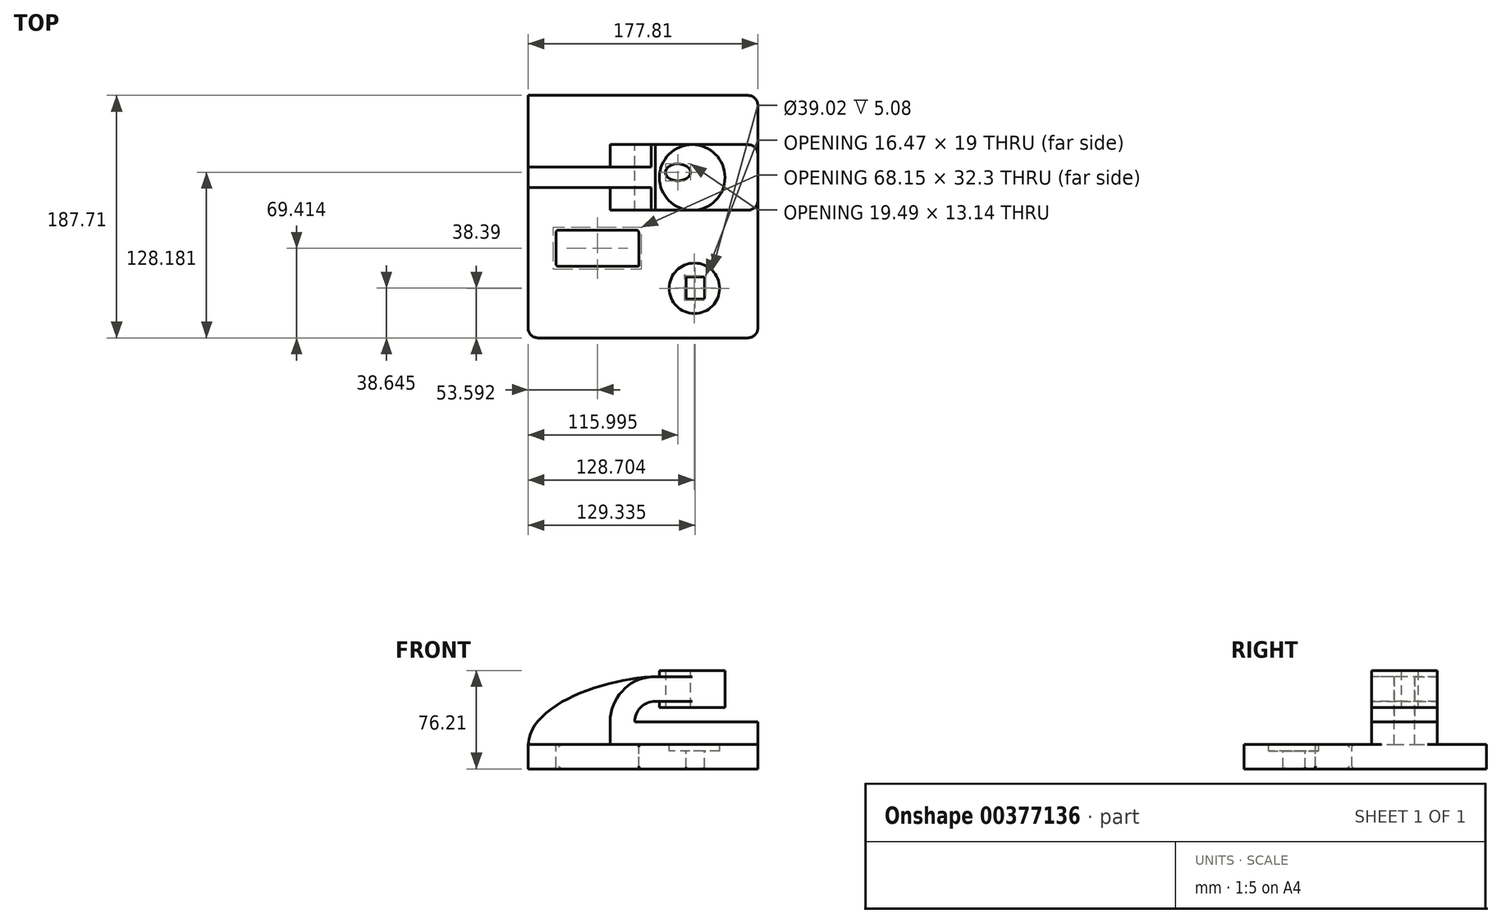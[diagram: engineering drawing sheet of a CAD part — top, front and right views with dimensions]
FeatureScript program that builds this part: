
annotation { "Feature Type Name" : "Feature", "Feature Type Description" : "" }
export const myFeature = defineFeature(function(context is Context, id is Id, definition is map)
    precondition{}
    {
        {
            var Q0;
            Q0=qCreatedBy(makeId("Front.planeOp"),FACE);
            var sketch = newSketch(context, id + "F0", { "sketchPlane" : qUnion([Q0])});
            skLineSegment(sketch, "E0.rect.bottom", {"start": v(-41.28, 9.52) * mm, "end": v(41.28, 9.52) * mm});
            skLineSegment(sketch, "E0.rect.top", {"start": v(-41.28, -9.52) * mm, "end": v(41.28, -9.52) * mm});
            skLineSegment(sketch, "E0.rect.left", {"start": v(-41.28, 9.52) * mm, "end": v(-41.28, -9.52) * mm});
            skLineSegment(sketch, "E0.rect.right", {"start": v(41.28, 9.52) * mm, "end": v(41.28, -9.52) * mm});
            skPoint(sketch, "E0.rect.middle", {"position": v(0, 0) * mm});
            skLineSegment(sketch, "E1", {"start": v(41.28, 9.52) * mm, "end": v(41.28, 27) * mm});
            skArc(sketch, "E2", {"start": v(41.28, 27) * mm, "mid": v(45.92, 38.23) * mm, "end": v(57.15, 42.88) * mm});
            skLineSegment(sketch, "E3", {"start": v(57.15, 42.88) * mm, "end": v(85.72, 42.88) * mm});
            skLineSegment(sketch, "E4.rect.bottom", {"start": v(60.32, 38.1) * mm, "end": v(111.12, 38.1) * mm});
            skLineSegment(sketch, "E4.rect.top", {"start": v(60.32, 66.68) * mm, "end": v(111.12, 66.68) * mm});
            skLineSegment(sketch, "E4.rect.left", {"start": v(60.32, 38.1) * mm, "end": v(60.32, 66.68) * mm});
            skLineSegment(sketch, "E4.rect.right", {"start": v(111.13, 38.1) * mm, "end": v(111.12, 66.68) * mm});
            skPoint(sketch, "E4.rect.middle", {"position": v(85.72, 52.39) * mm});
            skLineSegment(sketch, "E5.0", {"start": v(57.15, 61.93) * mm, "end": v(85.72, 61.93) * mm});
            skArc(sketch, "E5.1", {"start": v(22.23, 27) * mm, "mid": v(32.45, 51.7) * mm, "end": v(57.15, 61.93) * mm});
            skLineSegment(sketch, "E5.2", {"start": v(22.23, 9.52) * mm, "end": v(22.23, 27) * mm});
            skLineSegment(sketch, "E6", {"start": v(85.72, 38.1) * mm, "end": v(85.72, 66.68) * mm});
            skFitSpline(sketch, "E7", {"points": [v(-41.28, 9.53) * mm, v(57.15, 61.93) * mm], "startDerivative": vector(5.2, 92.34) * mm, "endDerivative": vector(120.92, 4.22) * mm});
            skSolve(sketch);
        }
        {
            var Q0;
            Q0=makeQuery(id+"F0.imprint","IMPRINT",FACE,{"disambiguationData":[TD([[makeQuery(id+"F0.imprint","IMPRINT",EDGE,{"derivedFrom":sQuery(id+"F0.wireOp",EDGE,"E0.rect.top")}),1.0]])]});
            extrude(context, id + "F1", {"entities" : qUnion([Q0]), "endBound" : BoundingType.SYMMETRIC, "depth" : 127 * mm});
        }
        {
            var Q0;
            {var subQ9=sQuery(id+"F0.wireOp",EDGE,"E1");Q0=makeQuery(id+"F0.imprint","IMPRINT",FACE,{"disambiguationData":[TD([[makeQuery(id+"F0.imprint","IMPRINT",EDGE,{"derivedFrom":subQ9}),1.0]])]});}
            var Q1;
            {var subQ0=sQuery(id+"F0.wireOp",EDGE,"E6");var subQ1=sQuery(id+"F0.wireOp",EDGE,"E3");var subQ2=makeQuery(id+"F0.imprint","INTERSECT",VERTEX,{"derivedFrom":[subQ1,subQ0]});Q1=makeQuery(id+"F0.imprint","IMPRINT",FACE,{"disambiguationData":[TD([[makeQuery(id+"F0.imprint","IMPRINT",EDGE,{"disambiguationData":[TD([[subQ2,1.0]])],"derivedFrom":subQ1}),1.0]])]});}
            extrude(context, id + "F2", {"entities" : qUnion([Q0, Q1]), "operationType" : NewBodyOperationType.ADD, "endBound" : BoundingType.SYMMETRIC, "depth" : 50.8 * mm});
        }
        {
            var Q0;
            {var subQ3=sQuery(id+"F0.wireOp",EDGE,"E5.2");Q0=makeQuery(id+"F0.imprint","IMPRINT",FACE,{"disambiguationData":[TD([[makeQuery(id+"F0.imprint","IMPRINT",EDGE,{"derivedFrom":subQ3}),1.0]])]});}
            extrude(context, id + "F3", {"entities" : qUnion([Q0]), "operationType" : NewBodyOperationType.ADD, "endBound" : BoundingType.SYMMETRIC, "depth" : 15.88 * mm});
        }
        {
            var Q0;
            {var subQ5=sQuery(id+"F0.wireOp",EDGE,"E4.rect.right");Q0=makeQuery(id+"F0.imprint","IMPRINT",FACE,{"disambiguationData":[TD([[makeQuery(id+"F0.imprint","IMPRINT",EDGE,{"derivedFrom":subQ5}),1.0]])]});}
            var Q1;
            Q1=sQuery(id+"F0.wireOp",EDGE,"E6");
            revolve(context, id + "F4", {"operationType" : NewBodyOperationType.ADD, "entities" : qUnion([Q0]), "axis" : qUnion([Q1]), "revolveType" : RevolveType.FULL});
        }
        {
            var Q0;
            Q0=makeQuery(id+"F2.boolean.opBoolean","MERGE",FACE,{"derivedFrom":[makeQuery(id+"F1.opExtrude","SWEPT_FACE",FACE,{"disambiguationData":[OSD([sQuery(id+"F0.wireOp",EDGE,"E0.rect.right")])]}),makeQuery(id+"F2.opExtrude","SWEPT_FACE",FACE,{"disambiguationData":[OSD([sQuery(id+"F0.wireOp",EDGE,"E1")])]})]});
            extrude(context, id + "F5", {"entities" : qUnion([Q0]), "operationType" : NewBodyOperationType.ADD, "depth" : 95.25 * mm});
        }
        {
            var Q0;
            {var subQ0=sQuery(id+"F0.wireOp",EDGE,"E0.rect.right");Q0=makeQuery(id+"F5.boolean.opBoolean","MERGE",FACE,{"derivedFrom":[makeQuery(id+"F1.opExtrude","CAP_FACE",FACE,{"disambiguationData":[OSD([sQuery(id+"F0.wireOp",EDGE,"E0.rect.bottom"),sQuery(id+"F0.wireOp",EDGE,"E0.rect.top"),sQuery(id+"F0.wireOp",EDGE,"E0.rect.left"),subQ0])],"isStart":false}),makeQuery(id+"F5.opExtrude","SWEPT_FACE",FACE,{"disambiguationData":[OSD([subQ0]),TDD([makeQuery(id+"F1.opExtrude","CAP_EDGE",EDGE,{"disambiguationData":[OSD([subQ0])],"isStart":false})])]})]});}
            extrude(context, id + "F6", {"entities" : qUnion([Q0]), "operationType" : NewBodyOperationType.ADD, "depth" : 60.7 * mm});
        }
        {
            var Q0;
            {var subQ0=sQuery(id+"F0.wireOp",EDGE,"E1");var subQ1=sQuery(id+"F0.wireOp",EDGE,"E0.rect.right");var subQ2=sQuery(id+"F0.wireOp",EDGE,"E0.rect.bottom");var subQ7=sQuery(id+"F0.wireOp",EDGE,"E0.rect.left");var subQ8=makeQuery(id+"F1.opExtrude","CAP_FACE",FACE,{"disambiguationData":[OSD([subQ2,sQuery(id+"F0.wireOp",EDGE,"E0.rect.top"),subQ7,subQ1])],"isStart":false});var subQ10=makeQuery(id+"F1.opExtrude","SWEPT_FACE",FACE,{"disambiguationData":[OSD([subQ2])]});Q0=makeQuery(id+"F6.boolean.opBoolean","MERGE",FACE,{"derivedFrom":[makeQuery(id+"F5.boolean.opBoolean","MERGE",FACE,{"derivedFrom":[makeQuery(id+"F3.boolean.opBoolean","SPLIT",FACE,{"disambiguationData":[TD([subQ8])],"derivedFrom":subQ10}),makeQuery(id+"F5.opExtrude","SWEPT_FACE",FACE,{"disambiguationData":[OSD([subQ2,subQ1,subQ0]),TDD([makeQuery(id+"F2.boolean.opBoolean","SPLIT",EDGE,{"disambiguationData":[TD([subQ8])],"derivedFrom":makeQuery(id+"F1.opExtrude","SWEPT_EDGE",EDGE,{"disambiguationData":[OSD([subQ2,subQ1,subQ0])]})})])]})]}),makeQuery(id+"F6.opExtrude","SWEPT_FACE",FACE,{"disambiguationData":[OSD([subQ2,subQ1,subQ0])]})]});}
            var sketch = newSketch(context, id + "F7", { "sketchPlane" : qUnion([Q0])});
            skLineSegment(sketch, "E8.bottom", {"start": v(44.37, -68.92) * mm, "end": v(-19.73, -68.92) * mm});
            skLineSegment(sketch, "E8.top", {"start": v(44.37, -40.68) * mm, "end": v(-19.73, -40.68) * mm});
            skLineSegment(sketch, "E8.left", {"start": v(44.37, -68.92) * mm, "end": v(44.37, -40.68) * mm});
            skLineSegment(sketch, "E8.right", {"start": v(-19.73, -68.92) * mm, "end": v(-19.73, -40.68) * mm});
            skPoint(sketch, "E8.middle", {"position": v(12.32, -54.8) * mm});
            skSolve(sketch);
        }
        {
            var Q0;
            Q0=makeQuery(id+"F7.imprint","IMPRINT",FACE,{"disambiguationData":[TD([[makeQuery(id+"F7.imprint","IMPRINT",EDGE,{"derivedFrom":sQuery(id+"F7.wireOp",EDGE,"E8.bottom")}),-1.0]])]});
            extrude(context, id + "F8", {"entities" : qUnion([Q0]), "operationType" : NewBodyOperationType.REMOVE, "oppositeDirection" : true, "depth" : 25.4 * mm});
        }
        {
            var Q0;
            {var subQ0=sQuery(id+"F0.wireOp",EDGE,"E1");var subQ1=sQuery(id+"F0.wireOp",EDGE,"E0.rect.right");var subQ2=sQuery(id+"F0.wireOp",EDGE,"E0.rect.bottom");var subQ7=sQuery(id+"F0.wireOp",EDGE,"E0.rect.left");var subQ8=makeQuery(id+"F1.opExtrude","CAP_FACE",FACE,{"disambiguationData":[OSD([subQ2,sQuery(id+"F0.wireOp",EDGE,"E0.rect.top"),subQ7,subQ1])],"isStart":false});var subQ10=makeQuery(id+"F1.opExtrude","SWEPT_FACE",FACE,{"disambiguationData":[OSD([subQ2])]});Q0=makeQuery(id+"F6.boolean.opBoolean","MERGE",FACE,{"derivedFrom":[makeQuery(id+"F5.boolean.opBoolean","MERGE",FACE,{"derivedFrom":[makeQuery(id+"F3.boolean.opBoolean","SPLIT",FACE,{"disambiguationData":[TD([subQ8])],"derivedFrom":subQ10}),makeQuery(id+"F5.opExtrude","SWEPT_FACE",FACE,{"disambiguationData":[OSD([subQ2,subQ1,subQ0]),TDD([makeQuery(id+"F2.boolean.opBoolean","SPLIT",EDGE,{"disambiguationData":[TD([subQ8])],"derivedFrom":makeQuery(id+"F1.opExtrude","SWEPT_EDGE",EDGE,{"disambiguationData":[OSD([subQ2,subQ1,subQ0])]})})])]})]}),makeQuery(id+"F6.opExtrude","SWEPT_FACE",FACE,{"disambiguationData":[OSD([subQ2,subQ1,subQ0])]})]});}
            var sketch = newSketch(context, id + "F9", { "sketchPlane" : qUnion([Q0])});
            skCircle(sketch, "E9", {"center": v(87.42, -85.82) * mm, "radius": 19.5 * mm});
            skPoint(sketch, "E9.first.point", {"position": v(99.6, -70.58) * mm});
            skPoint(sketch, "E9.second.point", {"position": v(68.56, -90.8) * mm});
            skPoint(sketch, "E9.third.point", {"position": v(68.2, -82.5) * mm});
            skSolve(sketch);
        }
        {
            var Q0;
            Q0=makeQuery(id+"F9.imprint","IMPRINT",FACE,{"disambiguationData":[TD([[makeQuery(id+"F9.imprint","IMPRINT",EDGE,{"derivedFrom":sQuery(id+"F9.wireOp",EDGE,"E9")}),1.0]])]});
            extrude(context, id + "F10", {"entities" : qUnion([Q0]), "operationType" : NewBodyOperationType.REMOVE, "oppositeDirection" : true, "depth" : 5.08 * mm});
        }
        {
            var Q0;
            {var subQ0=sQuery(id+"F0.wireOp",EDGE,"E1");var subQ1=sQuery(id+"F0.wireOp",EDGE,"E0.rect.right");var subQ2=sQuery(id+"F0.wireOp",EDGE,"E0.rect.bottom");var subQ7=sQuery(id+"F0.wireOp",EDGE,"E0.rect.left");var subQ8=makeQuery(id+"F1.opExtrude","CAP_FACE",FACE,{"disambiguationData":[OSD([subQ2,sQuery(id+"F0.wireOp",EDGE,"E0.rect.top"),subQ7,subQ1])],"isStart":false});var subQ10=makeQuery(id+"F1.opExtrude","SWEPT_FACE",FACE,{"disambiguationData":[OSD([subQ2])]});Q0=makeQuery(id+"F6.boolean.opBoolean","MERGE",FACE,{"derivedFrom":[makeQuery(id+"F5.boolean.opBoolean","MERGE",FACE,{"derivedFrom":[makeQuery(id+"F3.boolean.opBoolean","SPLIT",FACE,{"disambiguationData":[TD([subQ8])],"derivedFrom":subQ10}),makeQuery(id+"F5.opExtrude","SWEPT_FACE",FACE,{"disambiguationData":[OSD([subQ2,subQ1,subQ0]),TDD([makeQuery(id+"F2.boolean.opBoolean","SPLIT",EDGE,{"disambiguationData":[TD([subQ8])],"derivedFrom":makeQuery(id+"F1.opExtrude","SWEPT_EDGE",EDGE,{"disambiguationData":[OSD([subQ2,subQ1,subQ0])]})})])]})]}),makeQuery(id+"F6.opExtrude","SWEPT_FACE",FACE,{"disambiguationData":[OSD([subQ2,subQ1,subQ0])]})]});}
            var sketch = newSketch(context, id + "F11", { "sketchPlane" : qUnion([Q0])});
            skLineSegment(sketch, "E10.bottom", {"start": v(95.28, -77.08) * mm, "end": v(80.84, -77.08) * mm});
            skLineSegment(sketch, "E10.top", {"start": v(95.28, -94.05) * mm, "end": v(80.84, -94.05) * mm});
            skLineSegment(sketch, "E10.left", {"start": v(95.28, -77.08) * mm, "end": v(95.28, -94.05) * mm});
            skLineSegment(sketch, "E10.right", {"start": v(80.84, -77.08) * mm, "end": v(80.84, -94.05) * mm});
            skSolve(sketch);
        }
        {
            var Q0;
            Q0=makeQuery(id+"F11.imprint","IMPRINT",FACE,{"disambiguationData":[TD([[makeQuery(id+"F11.imprint","IMPRINT",EDGE,{"derivedFrom":sQuery(id+"F11.wireOp",EDGE,"E10.bottom")}),1.0]])]});
            extrude(context, id + "F12", {"entities" : qUnion([Q0]), "operationType" : NewBodyOperationType.REMOVE, "oppositeDirection" : true, "depth" : 25.4 * mm});
        }
        {
            var Q0;
            Q0=makeQuery(id+"F4.opRevolve","SWEPT_FACE",FACE,{"disambiguationData":[OSD([sQuery(id+"F0.wireOp",EDGE,"E4.rect.top")])]});
            var sketch = newSketch(context, id + "F13", { "sketchPlane" : qUnion([Q0])});
            skEllipse(sketch, "E11", {"center": v(74.71, 3.97) * mm, "majorRadius": 9.75 * mm, "minorRadius": 6.57 * mm, "majorAxis": v(1, 0)});
            skSolve(sketch);
        }
        {
            var Q0;
            Q0=makeQuery(id+"F13.imprint","IMPRINT",FACE,{"disambiguationData":[TD([[makeQuery(id+"F13.imprint","IMPRINT",EDGE,{"derivedFrom":sQuery(id+"F13.wireOp",EDGE,"E11")}),1.0]])]});
            var Q1;
            Q1=sQuery(id+"F13.wireOp",EDGE,"E11");
            extrude(context, id + "F14", {"entities" : qUnion([Q0]), "operationType" : NewBodyOperationType.REMOVE, "surfaceEntities" : qUnion([Q1]), "endBound" : BoundingType.UP_TO_NEXT, "oppositeDirection" : true, "depth" : 25.4 * mm});
        }
        {
            var Q0;
            Q0=makeQuery(id+"F6.opExtrude","CAP_EDGE",EDGE,{"disambiguationData":[OSD([sQuery(id+"F0.wireOp",EDGE,"E0.rect.left")])],"isStart":false});
            var Q1;
            Q1=makeQuery(id+"F6.opExtrude","CAP_EDGE",EDGE,{"disambiguationData":[OSD([sQuery(id+"F0.wireOp",EDGE,"E0.rect.right")])],"isStart":false});
            var Q2;
            {var subQ0=sQuery(id+"F0.wireOp",EDGE,"E1");Q2=makeQuery(id+"F5.opExtrude","CAP_EDGE",EDGE,{"disambiguationData":[OSD([subQ0]),TDD([makeQuery(id+"F2.opExtrude","CAP_EDGE",EDGE,{"disambiguationData":[OSD([subQ0])],"isStart":false})])],"isStart":false});}
            var Q3;
            {var subQ0=sQuery(id+"F0.wireOp",EDGE,"E1");Q3=makeQuery(id+"F5.opExtrude","CAP_EDGE",EDGE,{"disambiguationData":[OSD([subQ0]),TDD([makeQuery(id+"F2.opExtrude","CAP_EDGE",EDGE,{"disambiguationData":[OSD([subQ0])],"isStart":true})])],"isStart":false});}
            var Q4;
            {var subQ0=sQuery(id+"F0.wireOp",EDGE,"E0.rect.right");Q4=makeQuery(id+"F5.opExtrude","CAP_EDGE",EDGE,{"disambiguationData":[OSD([subQ0]),TDD([makeQuery(id+"F1.opExtrude","CAP_EDGE",EDGE,{"disambiguationData":[OSD([subQ0])],"isStart":true})])],"isStart":false});}
            fillet(context, id + "F15", {"entities" : qUnion([Q0, Q1, Q2, Q3, Q4]), "radius" : 7.62 * mm, "tangentPropagation" : true, "allowEdgeOverflow" : false});
        }
        {
            var Q0;
            Q0=makeQuery(id+"F8.boolean.opBoolean","COPY",FACE,{"derivedFrom":makeQuery(id+"F8.opExtrude","SWEPT_FACE",FACE,{"disambiguationData":[OSD([sQuery(id+"F7.wireOp",EDGE,"E8.right")])]})});
            var Q1;
            Q1=makeQuery(id+"F8.boolean.opBoolean","COPY",FACE,{"derivedFrom":makeQuery(id+"F8.opExtrude","SWEPT_FACE",FACE,{"disambiguationData":[OSD([sQuery(id+"F7.wireOp",EDGE,"E8.top")])]})});
            fillet(context, id + "F16", {"entities" : qUnion([Q0, Q1]), "radius" : 2.03 * mm, "tangentPropagation" : true, "allowEdgeOverflow" : false});
        }
        {
            var Q0;
            Q0=makeQuery(id+"F12.boolean.opBoolean","INTERSECT",EDGE,{"derivedFrom":[makeQuery(id+"F10.boolean.opBoolean","COPY",FACE,{"derivedFrom":makeQuery(id+"F10.opExtrude","CAP_FACE",FACE,{"disambiguationData":[OSD([sQuery(id+"F9.wireOp",EDGE,"E9")])],"isStart":false})}),makeQuery(id+"F12.opExtrude","SWEPT_FACE",FACE,{"disambiguationData":[OSD([sQuery(id+"F11.wireOp",EDGE,"E10.bottom")])]})]});
            var Q1;
            Q1=makeQuery(id+"F12.boolean.opBoolean","COPY",FACE,{"derivedFrom":makeQuery(id+"F12.opExtrude","SWEPT_FACE",FACE,{"disambiguationData":[OSD([sQuery(id+"F11.wireOp",EDGE,"E10.left")])]})});
            var Q2;
            Q2=makeQuery(id+"F12.boolean.opBoolean","INTERSECT",EDGE,{"derivedFrom":[makeQuery(id+"F10.boolean.opBoolean","COPY",FACE,{"derivedFrom":makeQuery(id+"F10.opExtrude","CAP_FACE",FACE,{"disambiguationData":[OSD([sQuery(id+"F9.wireOp",EDGE,"E9")])],"isStart":false})}),makeQuery(id+"F12.opExtrude","SWEPT_FACE",FACE,{"disambiguationData":[OSD([sQuery(id+"F11.wireOp",EDGE,"E10.right")])]})]});
            var Q3;
            Q3=makeQuery(id+"F12.boolean.opBoolean","COPY",FACE,{"derivedFrom":makeQuery(id+"F12.opExtrude","SWEPT_FACE",FACE,{"disambiguationData":[OSD([sQuery(id+"F11.wireOp",EDGE,"E10.top")])]})});
            fillet(context, id + "F17", {"entities" : qUnion([Q0, Q1, Q2, Q3]), "radius" : 1.02 * mm, "tangentPropagation" : true, "allowEdgeOverflow" : false});
        }
    });
